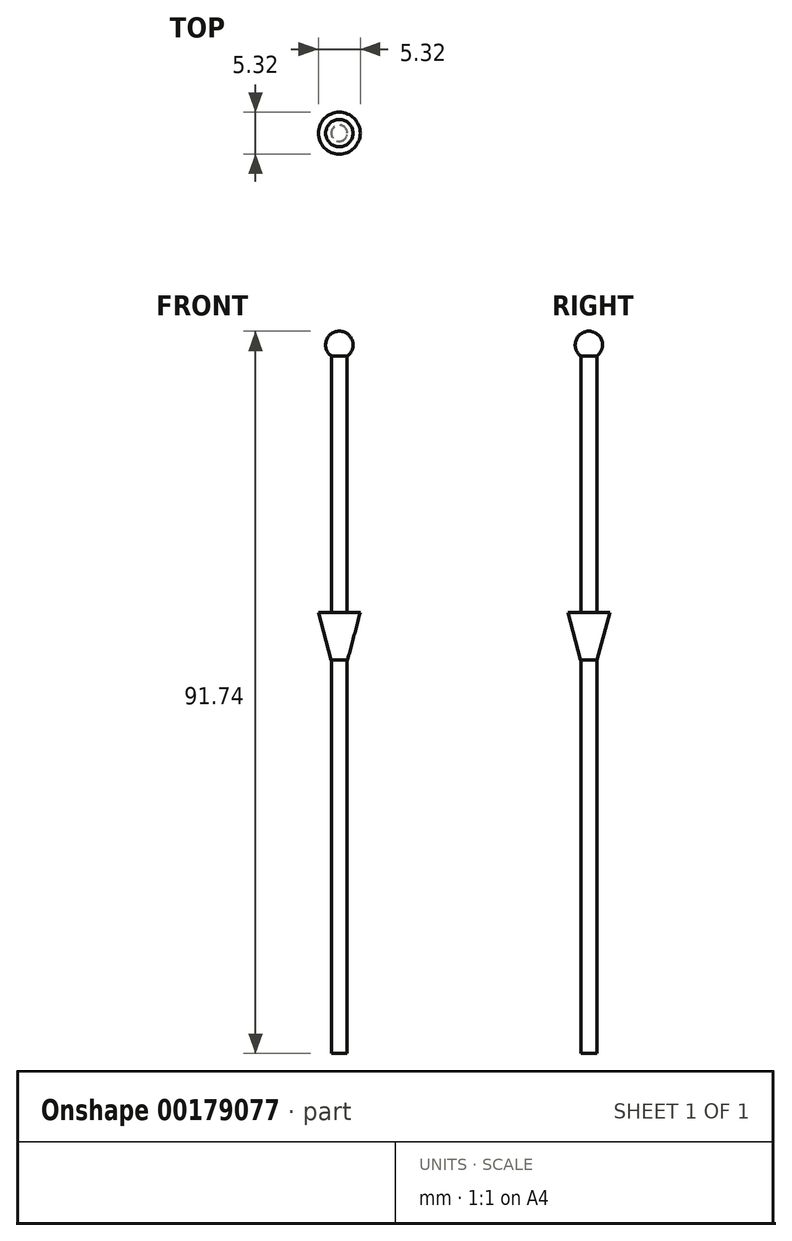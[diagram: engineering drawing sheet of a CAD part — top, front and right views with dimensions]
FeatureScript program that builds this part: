
annotation { "Feature Type Name" : "Feature", "Feature Type Description" : "" }
export const myFeature = defineFeature(function(context is Context, id is Id, definition is map)
    precondition{}
    {
        {
            var Q0;
            Q0=qCreatedBy(makeId("Top.planeOp"),FACE);
            var sketch = newSketch(context, id + "F0", { "sketchPlane" : qUnion([Q0])});
            skCircle(sketch, "E0", {"center": v(-2.72, 0.65) * mm, "radius": 1 * mm});
            skSolve(sketch);
        }
        {
            var Q0;
            Q0=makeQuery(id+"F0.imprint","IMPRINT",FACE,{"disambiguationData":[TD([[makeQuery(id+"F0.imprint","IMPRINT",EDGE,{"derivedFrom":sQuery(id+"F0.wireOp",EDGE,"E0")}),1.0]])]});
            extrude(context, id + "F1", {"entities" : qUnion([Q0]), "depth" : 90 * mm});
        }
        {
            var Q0;
            Q0=makeQuery(id+"F1.opExtrude","CAP_FACE",FACE,{"disambiguationData":[OSD([sQuery(id+"F0.wireOp",EDGE,"E0")])],"isStart":false});
            var sketch = newSketch(context, id + "F2", { "sketchPlane" : qUnion([Q0])});
            skLineSegment(sketch, "E1.left", {"start": v(-2.72, 2.39) * mm, "end": v(-2.72, -1.1) * mm});
            skArc(sketch, "E2", {"start": v(-2.72, -1.1) * mm, "mid": v(-0.98, 0.65) * mm, "end": v(-2.72, 2.39) * mm});
            skPoint(sketch, "E3.orphan", {"position": v(-2.72, 1.65) * mm});
            skPoint(sketch, "E4.orphan", {"position": v(-2.72, -0.35) * mm});
            skSolve(sketch);
        }
        {
            var Q0;
            {var subQ0=sQuery(id+"F2.wireOp",EDGE,"E2");Q0=makeQuery(id+"F2.imprint","IMPRINT",FACE,{"disambiguationData":[TD([[makeQuery(id+"F2.imprint","IMPRINT",EDGE,{"derivedFrom":subQ0}),1.0]])]});}
            var Q1;
            {var subQ0=sQuery(id+"F2.wireOp",EDGE,"E1.left");var subQ1=makeQuery(id+"F1.opExtrude","CAP_EDGE",EDGE,{"disambiguationData":[OSD([sQuery(id+"F0.wireOp",EDGE,"E0")])],"isStart":false});var subQ2=makeQuery(id+"F2.imprint","INTERSECT",VERTEX,{"disambiguationData":[OD(0.0)],"derivedFrom":[subQ1,subQ0]});Q1=makeQuery(id+"F2.imprint","IMPRINT",FACE,{"disambiguationData":[TD([[makeQuery(id+"F2.imprint","IMPRINT",EDGE,{"disambiguationData":[TD([[subQ2,-1.0]])],"derivedFrom":subQ0}),1.0]])]});}
            var Q2;
            Q2=sQuery(id+"F2.wireOp",EDGE,"E1.left");
            revolve(context, id + "F3", {"operationType" : NewBodyOperationType.ADD, "entities" : qUnion([Q0, Q1]), "axis" : qUnion([Q2]), "revolveType" : RevolveType.FULL});
        }
        {
            var Q0;
            Q0=qCreatedBy(makeId("Top.planeOp"),FACE);
            cPlane(context, id + "F4", {"entities" : qUnion([Q0]), "cplaneType" : CPlaneType.OFFSET, "offset" : 50 * mm, "width" : 150 * mm, "height" : 150 * mm});
        }
        {
            var Q0;
            Q0=qCreatedBy(id+"F4.planeOp",FACE);
            var sketch = newSketch(context, id + "F5", { "sketchPlane" : qUnion([Q0])});
            skCircle(sketch, "E5.0", {"center": v(-2.72, 0.65) * mm, "radius": 1 * mm});
            skCircle(sketch, "E6", {"center": v(-2.72, 0.65) * mm, "radius": 1.05 * mm});
            skSolve(sketch);
        }
        {
            var Q0;
            Q0=makeQuery(id+"F5.imprint","IMPRINT",FACE,{"disambiguationData":[TD([[makeQuery(id+"F5.imprint","IMPRINT",EDGE,{"derivedFrom":sQuery(id+"F5.wireOp",EDGE,"E5.0")}),-1.0]])]});
            extrude(context, id + "F6", {"entities" : qUnion([Q0]), "operationType" : NewBodyOperationType.ADD, "depth" : 6 * mm, "hasDraft" : true, "draftAngle" : 15 * degree});
        }
    });
